# Revit family: Partition-Bobrick-Evolve
name_source: partatom
category: Specialty Equipment
revit_build: Autodesk Revit 2015 (Build: 20140606_1530(x64)
units: mm (PartAtom-declared; Revit-internal decimal feet)

## types (5) — shared parameters
3 - Right Hinged Inswing = No
9" Clearance Option = Yes
Assembly Code = C1010
Clearance Height = 9"
Default Elevation = 48"
Description = Evolve Toilet Partition
Door Height = 72"
Door Height Constraint = 72"
Door Panel = Yes
Door Width = 27 3/8"
Exterior Finish = Laminate-Bobrick-White
Hardware Material = Stainless Steel-Bobrick-Satin
Head Rail Length = 1 1/8"
Installation Type = Floor-Anchored
Interior Finish = Laminate-Bobrick-White
Left Partition = No
Length = 60"
Manufacturer = Bobrick
Overall Height = 82 1/8"
Partition Length Constraint = 59 13/16"
Price = Prices may vary. Please consult Manufacturer Representative for most up-to-date price list.
Right Stile Option = Yes

## per-type parameters (varying)
- Left Corner Partition: 1 - Left Hinged Inswing=No; 2 - Left Hinged Outswing=Yes; 4 - Right Hinged Outswing=No; Center Stall Constraint=48"; Center Stall Option=No; Center Stall Width=63 3/8"; Corner Option=Yes; Corner Stall Constraint=63 3/8"; Corner Stall Width=63 3/8"; Door Option=2; Inswing Visibility=No; Left Hinge=Yes; Left Stile Constraint=48"; Left Stile Option=Yes; Left Stile Width=60"; Model=Privada Floor-Anchored Toilet Compartment; Product Documentation Link=http://www.privadapartitions.com; Product Page URL=http://www.privadapartitions.com; Right Hinge=No; Right Partition=Yes; Right Side Corner=No; Right Stile Constraint=12"; Right Stile Width=12"; Stall Width Constraint=63 3/8"; URL=http://www.privadapartitions.com; Warranty Information=10 Year Warranty
- Center Partition: 1 - Left Hinged Inswing=Yes; 2 - Left Hinged Outswing=No; 4 - Right Hinged Outswing=No; Center Stall Constraint=32 7/8"; Center Stall Option=Yes; Center Stall Width=32 7/8"; Corner Option=No; Corner Stall Constraint=32 7/8"; Corner Stall Width=32 7/8"; Door Option=1; Inswing Visibility=Yes; Left Hinge=Yes; Left Stile Constraint=5 1/2"; Left Stile Option=No; Left Stile Width=5 1/2"; Model=Evolve Toilet Partition; Product Page URL=http://www.bobrick.com; Right Hinge=No; Right Partition=Yes; Right Side Corner=No; Right Stile Constraint=5 1/2"; Right Stile Width=5 1/2"; Stall Width Constraint=32 7/8"; URL=http://www.bobrick.com
- Right Corner Partition: 1 - Left Hinged Inswing=No; 2 - Left Hinged Outswing=No; 4 - Right Hinged Outswing=Yes; Center Stall Constraint=48"; Center Stall Option=Yes; Center Stall Width=63 3/8"; Corner Option=No; Corner Stall Constraint=63 3/8"; Corner Stall Width=63 3/8"; Door Option=4; Inswing Visibility=No; Left Hinge=No; Left Stile Constraint=12"; Left Stile Option=No; Left Stile Width=12"; Model=Privada Floor-Anchored Toilet Compartment; Product Documentation Link=http://www.privadapartitions.com; Product Page URL=http://www.privadapartitions.com; Right Hinge=Yes; Right Partition=No; Right Side Corner=Yes; Right Stile Constraint=48"; Right Stile Width=60"; Stall Width Constraint=63 3/8"; URL=http://www.privadapartitions.com; Warranty Information=10 Year Warranty
- Right Alcove: 1 - Left Hinged Inswing=Yes; 2 - Left Hinged Outswing=No; 4 - Right Hinged Outswing=No; Center Stall Constraint=32 7/8"; Center Stall Option=Yes; Center Stall Width=32 7/8"; Corner Option=No; Corner Stall Constraint=32 7/8"; Corner Stall Width=32 7/8"; Door Option=1; Inswing Visibility=Yes; Left Hinge=Yes; Left Stile Constraint=5 1/2"; Left Stile Option=No; Left Stile Width=5 1/2"; Model=Privada Floor-Anchored Toilet Compartment; Product Documentation Link=http://www.privadapartitions.com; Product Page URL=http://www.privadapartitions.com; Right Hinge=No; Right Partition=No; Right Side Corner=No; Right Stile Constraint=5 1/2"; Right Stile Width=5 1/2"; Stall Width Constraint=32 7/8"; URL=http://www.privadapartitions.com; Warranty Information=10 Year Warranty
- Left Alcove: 1 - Left Hinged Inswing=Yes; 2 - Left Hinged Outswing=No; 4 - Right Hinged Outswing=No; Center Stall Constraint=32 7/8"; Center Stall Option=Yes; Center Stall Width=32 7/8"; Corner Option=No; Corner Stall Constraint=32 7/8"; Corner Stall Width=32 7/8"; Door Option=1; Inswing Visibility=Yes; Left Hinge=Yes; Left Stile Constraint=5 1/2"; Left Stile Option=Yes; Left Stile Width=5 1/2"; Model=Privada Floor-Anchored Toilet Compartment; Product Documentation Link=http://www.privadapartitions.com; Product Page URL=http://www.privadapartitions.com; Right Hinge=No; Right Partition=Yes; Right Side Corner=No; Right Stile Constraint=5 1/2"; Right Stile Width=5 1/2"; Stall Width Constraint=32 7/8"; URL=http://www.privadapartitions.com; Warranty Information=10 Year Warranty

## geometry (parser evidence)
native form markers: Sweep x8
no freeform markers — native parametric forms only
